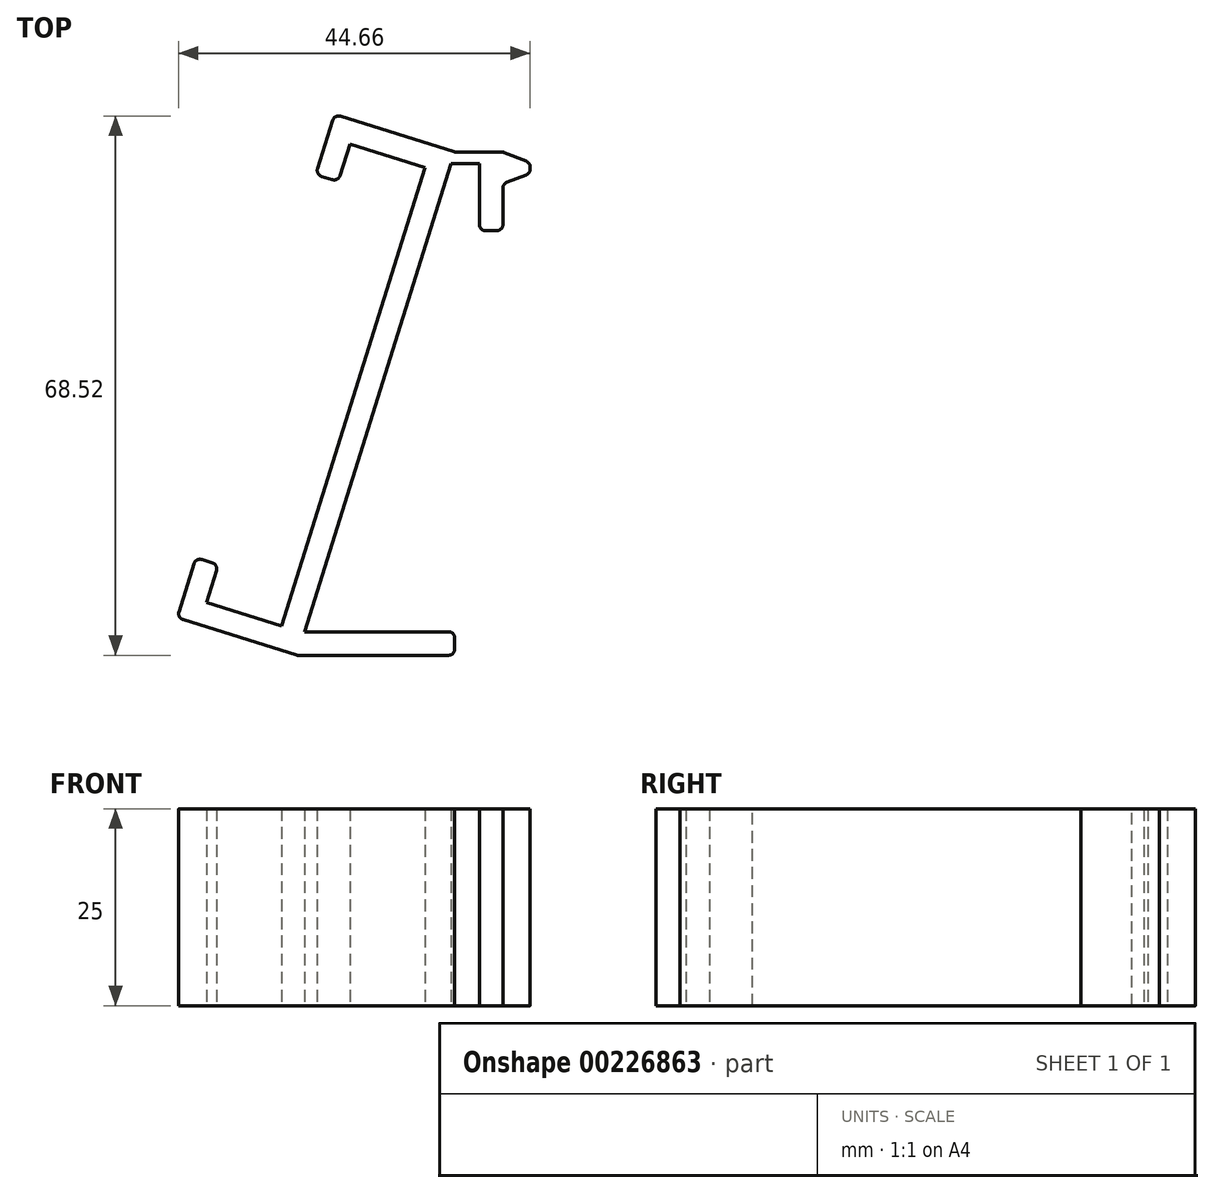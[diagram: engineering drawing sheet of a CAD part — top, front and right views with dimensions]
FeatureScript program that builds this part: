
annotation { "Feature Type Name" : "Feature", "Feature Type Description" : "" }
export const myFeature = defineFeature(function(context is Context, id is Id, definition is map)
    precondition{}
    {
        {
            var Q0;
            Q0=qCreatedBy(makeId("Top.planeOp"),FACE);
            var sketch = newSketch(context, id + "F0", { "sketchPlane" : qUnion([Q0])});
            skLineSegment(sketch, "E0", {"start": v(-17.66, -2.86) * mm, "end": v(-15.27, 4.78) * mm});
            skLineSegment(sketch, "E1", {"start": v(-15.27, 4.78) * mm, "end": v(0, 0) * mm});
            skLineSegment(sketch, "E2", {"start": v(-0.47, -1.5) * mm, "end": v(-20, -63.95) * mm});
            skLineSegment(sketch, "E3", {"start": v(-20, -63.95) * mm, "end": v(-35.27, -59.17) * mm});
            skLineSegment(sketch, "E4", {"start": v(-35.27, -59.17) * mm, "end": v(-32.88, -51.53) * mm});
            skLineSegment(sketch, "E5.0", {"start": v(-31.51, -57.2) * mm, "end": v(-30.02, -52.43) * mm});
            skLineSegment(sketch, "E5.1", {"start": v(-21.97, -60.19) * mm, "end": v(-31.51, -57.2) * mm});
            skLineSegment(sketch, "E5.2", {"start": v(-3.76, -1.97) * mm, "end": v(-21.97, -60.19) * mm});
            skLineSegment(sketch, "E6.0", {"start": v(-13.3, 1.02) * mm, "end": v(-3.76, -1.97) * mm});
            skLineSegment(sketch, "E6.1", {"start": v(-14.8, -3.75) * mm, "end": v(-13.3, 1.02) * mm});
            skLineSegment(sketch, "E7", {"start": v(-14.8, -3.75) * mm, "end": v(-17.66, -2.86) * mm});
            skLineSegment(sketch, "E8", {"start": v(-30.02, -52.43) * mm, "end": v(-32.88, -51.53) * mm});
            skLineSegment(sketch, "E9", {"start": v(0, 0) * mm, "end": v(0, 0) * mm});
            skLineSegment(sketch, "E10", {"start": v(0, 0) * mm, "end": v(6.13, 0) * mm});
            skLineSegment(sketch, "E11", {"start": v(6.13, 0) * mm, "end": v(6.13, -10) * mm});
            skLineSegment(sketch, "E12", {"start": v(6.13, -10) * mm, "end": v(3.13, -10) * mm});
            skLineSegment(sketch, "E13", {"start": v(3.13, -10) * mm, "end": v(3.13, -1.5) * mm});
            skLineSegment(sketch, "E14", {"start": v(3.13, -1.5) * mm, "end": v(-0.47, -1.5) * mm});
            skLineSegment(sketch, "E15", {"start": v(-20, -63.95) * mm, "end": v(0, -63.95) * mm});
            skLineSegment(sketch, "E16", {"start": v(0, -63.95) * mm, "end": v(0, -60.95) * mm});
            skLineSegment(sketch, "E17", {"start": v(0, -60.95) * mm, "end": v(-19.06, -60.95) * mm});
            skPoint(sketch, "E18.orphan", {"position": v(-20, -60.95) * mm});
            skLineSegment(sketch, "E19", {"start": v(6.13, 0) * mm, "end": v(9.6, -1.39) * mm});
            skLineSegment(sketch, "E20", {"start": v(9.6, -1.39) * mm, "end": v(9.6, -2.72) * mm});
            skLineSegment(sketch, "E21", {"start": v(9.6, -2.72) * mm, "end": v(6.13, -4.03) * mm});
            skSolve(sketch);
        }
        {
            var Q0;
            Q0=makeQuery(id+"F0.imprint","IMPRINT",FACE,{"disambiguationData":[TD([[makeQuery(id+"F0.imprint","IMPRINT",EDGE,{"derivedFrom":sQuery(id+"F0.wireOp",EDGE,"E0")}),-1.0]])]});
            var Q1;
            Q1=makeQuery(id+"F0.imprint","IMPRINT",FACE,{"disambiguationData":[TD([[makeQuery(id+"F0.imprint","IMPRINT",EDGE,{"derivedFrom":sQuery(id+"F0.wireOp",EDGE,"PnlH5BBP-SMww-GN2e-7UIA-jDxpLRwqYyTG")}),1.0]])]});
            var Q2;
            {var subQ0=sQuery(id+"F0.wireOp",EDGE,"E15");Q2=makeQuery(id+"F0.imprint","IMPRINT",FACE,{"disambiguationData":[TD([[makeQuery(id+"F0.imprint","IMPRINT",EDGE,{"derivedFrom":subQ0}),1.0]])]});}
            var Q3;
            {var subQ0=sQuery(id+"F0.wireOp",EDGE,"E19");Q3=makeQuery(id+"F0.imprint","IMPRINT",FACE,{"disambiguationData":[TD([[makeQuery(id+"F0.imprint","IMPRINT",EDGE,{"derivedFrom":subQ0}),-1.0]])]});}
            extrude(context, id + "F1", {"entities" : qUnion([Q0, Q1, Q2, Q3]), "depth" : 25 * mm});
        }
        {
            var Q0;
            Q0=makeQuery(id+"F1.opExtrude","SWEPT_EDGE",EDGE,{"disambiguationData":[OSD([sQuery(id+"F0.wireOp",EDGE,"E0"),sQuery(id+"F0.wireOp",EDGE,"E1")])]});
            var Q1;
            Q1=makeQuery(id+"F1.opExtrude","SWEPT_EDGE",EDGE,{"disambiguationData":[OSD([sQuery(id+"F0.wireOp",EDGE,"E0"),sQuery(id+"F0.wireOp",EDGE,"E1")])]});
            var Q2;
            Q2=makeQuery(id+"F1.opExtrude","SWEPT_EDGE",EDGE,{"disambiguationData":[OSD([sQuery(id+"F0.wireOp",EDGE,"E0"),sQuery(id+"F0.wireOp",EDGE,"E7")])]});
            var Q3;
            Q3=makeQuery(id+"F1.opExtrude","SWEPT_EDGE",EDGE,{"disambiguationData":[OSD([sQuery(id+"F0.wireOp",EDGE,"E6.1"),sQuery(id+"F0.wireOp",EDGE,"E7")])]});
            var Q4;
            Q4=makeQuery(id+"F1.opExtrude","SWEPT_EDGE",EDGE,{"disambiguationData":[OSD([sQuery(id+"F0.wireOp",EDGE,"E4"),sQuery(id+"F0.wireOp",EDGE,"E8")])]});
            var Q5;
            Q5=makeQuery(id+"F1.opExtrude","SWEPT_EDGE",EDGE,{"disambiguationData":[OSD([sQuery(id+"F0.wireOp",EDGE,"E3"),sQuery(id+"F0.wireOp",EDGE,"E4")])]});
            var Q6;
            Q6=makeQuery(id+"F1.opExtrude","SWEPT_EDGE",EDGE,{"disambiguationData":[OSD([sQuery(id+"F0.wireOp",EDGE,"E5.0"),sQuery(id+"F0.wireOp",EDGE,"E8")])]});
            var Q7;
            Q7=makeQuery(id+"F1.opExtrude","SWEPT_EDGE",EDGE,{"disambiguationData":[OSD([sQuery(id+"F0.wireOp",EDGE,"E2"),sQuery(id+"F0.wireOp",EDGE,"E3"),sQuery(id+"F0.wireOp",EDGE,"E15")])]});
            var Q8;
            Q8=makeQuery(id+"F1.opExtrude","SWEPT_EDGE",EDGE,{"disambiguationData":[OSD([sQuery(id+"F0.wireOp",EDGE,"E11"),sQuery(id+"F0.wireOp",EDGE,"E12")])]});
            var Q9;
            Q9=makeQuery(id+"F1.opExtrude","SWEPT_EDGE",EDGE,{"disambiguationData":[OSD([sQuery(id+"F0.wireOp",EDGE,"E12"),sQuery(id+"F0.wireOp",EDGE,"E13")])]});
            var Q10;
            Q10=makeQuery(id+"F1.opExtrude","SWEPT_EDGE",EDGE,{"disambiguationData":[OSD([sQuery(id+"F0.wireOp",EDGE,"E16"),sQuery(id+"F0.wireOp",EDGE,"E17")])]});
            var Q11;
            Q11=makeQuery(id+"F1.opExtrude","SWEPT_EDGE",EDGE,{"disambiguationData":[OSD([sQuery(id+"F0.wireOp",EDGE,"E15"),sQuery(id+"F0.wireOp",EDGE,"E16")])]});
            var Q12;
            Q12=makeQuery(id+"F1.opExtrude","SWEPT_EDGE",EDGE,{"disambiguationData":[OSD([sQuery(id+"F0.wireOp",EDGE,"E19"),sQuery(id+"F0.wireOp",EDGE,"E20")])]});
            var Q13;
            Q13=makeQuery(id+"F1.opExtrude","SWEPT_EDGE",EDGE,{"disambiguationData":[OSD([sQuery(id+"F0.wireOp",EDGE,"E20"),sQuery(id+"F0.wireOp",EDGE,"E21")])]});
            var Q14;
            Q14=makeQuery(id+"F1.opExtrude","SWEPT_EDGE",EDGE,{"disambiguationData":[OSD([sQuery(id+"F0.wireOp",EDGE,"E1"),sQuery(id+"F0.wireOp",EDGE,"E10")])]});
            var Q15;
            Q15=makeQuery(id+"F1.opExtrude","SWEPT_EDGE",EDGE,{"disambiguationData":[OSD([sQuery(id+"F0.wireOp",EDGE,"E10"),sQuery(id+"F0.wireOp",EDGE,"E11"),sQuery(id+"F0.wireOp",EDGE,"E19")])]});
            var Q16;
            Q16=makeQuery(id+"F1.opExtrude","SWEPT_EDGE",EDGE,{"disambiguationData":[OSD([sQuery(id+"F0.wireOp",EDGE,"E11"),sQuery(id+"F0.wireOp",EDGE,"E21")])]});
            fillet(context, id + "F2", {"entities" : qUnion([Q0, Q1, Q2, Q3, Q4, Q5, Q6, Q7, Q8, Q9, Q10, Q11, Q12, Q13, Q14, Q15, Q16]), "radius" : .8 * mm, "tangentPropagation" : true, "allowEdgeOverflow" : false});
        }
    });
